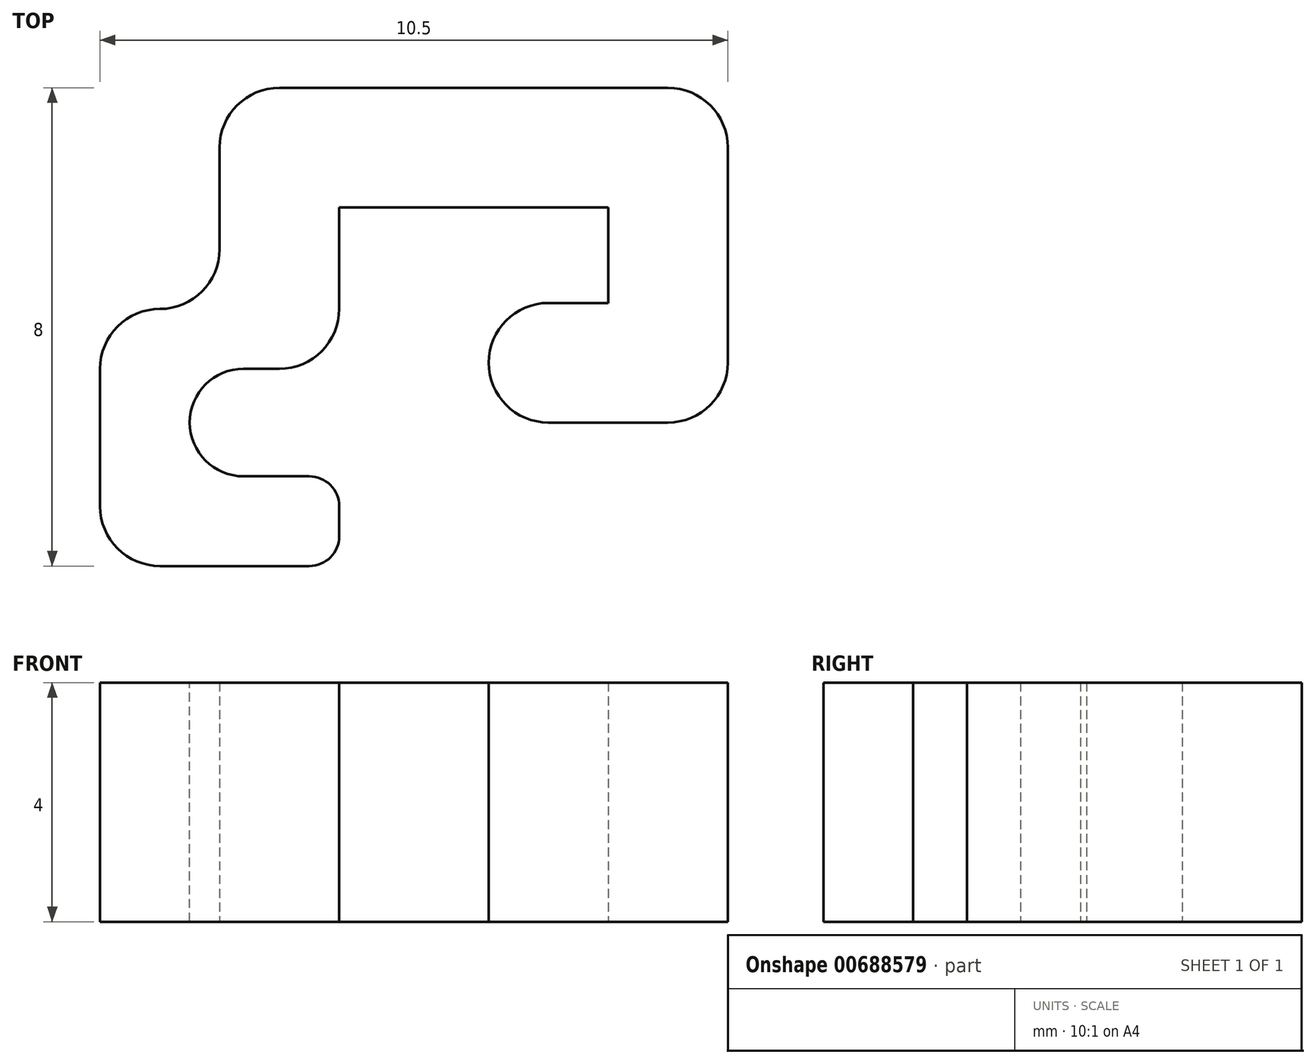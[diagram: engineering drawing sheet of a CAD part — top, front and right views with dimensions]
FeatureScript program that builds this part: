
annotation { "Feature Type Name" : "Feature", "Feature Type Description" : "" }
export const myFeature = defineFeature(function(context is Context, id is Id, definition is map)
    precondition{}
    {
        {
            var Q0;
            Q0=qCreatedBy(makeId("Top.planeOp"),FACE);
            var sketch = newSketch(context, id + "F0", { "sketchPlane" : qUnion([Q0])});
            skLineSegment(sketch, "E0", {"start": v(0, 0) * mm, "end": v(4.5, 0) * mm});
            skLineSegment(sketch, "E1", {"start": v(4.5, 0) * mm, "end": v(4.5, -1.6) * mm});
            skLineSegment(sketch, "E2", {"start": v(4.5, -1.6) * mm, "end": v(2.5, -1.6) * mm});
            skLineSegment(sketch, "E3", {"start": v(-2, 2) * mm, "end": v(6.5, 2) * mm});
            skLineSegment(sketch, "E4", {"start": v(6.5, 2) * mm, "end": v(6.5, -3.6) * mm});
            skLineSegment(sketch, "E5", {"start": v(6.5, -3.6) * mm, "end": v(2.5, -3.6) * mm});
            skLineSegment(sketch, "E6", {"start": v(2.5, -3.6) * mm, "end": v(2.5, -1.6) * mm});
            skLineSegment(sketch, "E7", {"start": v(0, 0) * mm, "end": v(0, -2.7) * mm});
            skLineSegment(sketch, "E8", {"start": v(0, -2.7) * mm, "end": v(-2.5, -2.7) * mm});
            skLineSegment(sketch, "E9", {"start": v(-2.5, -2.7) * mm, "end": v(-2.5, -4.5) * mm});
            skLineSegment(sketch, "E10", {"start": v(-2.5, -4.5) * mm, "end": v(0, -4.5) * mm});
            skLineSegment(sketch, "E11", {"start": v(0, -4.5) * mm, "end": v(0, -6) * mm});
            skLineSegment(sketch, "E12", {"start": v(0, -6) * mm, "end": v(-4, -6) * mm});
            skLineSegment(sketch, "E13", {"start": v(-4, -6) * mm, "end": v(-4, -1.7) * mm});
            skLineSegment(sketch, "E14", {"start": v(-4, -1.7) * mm, "end": v(-2, -1.7) * mm});
            skLineSegment(sketch, "E15", {"start": v(-2, -1.7) * mm, "end": v(-2, 2) * mm});
            skSolve(sketch);
        }
        {
            var Q0;
            Q0 = qSketchRegion(id + "F0", true);
            extrude(context, id + "F1", {"entities" : qUnion([Q0]), "depth" : 4 * mm, "offsetDistance" : 25 * mm});
        }
        {
            var Q0;
            Q0=makeQuery(id+"F1.opExtrude","SWEPT_EDGE",EDGE,{"disambiguationData":[OSD([sQuery(id+"F0.wireOp",EDGE,"E4"),sQuery(id+"F0.wireOp",EDGE,"E5")])]});
            var Q1;
            Q1=makeQuery(id+"F1.opExtrude","SWEPT_EDGE",EDGE,{"disambiguationData":[OSD([sQuery(id+"F0.wireOp",EDGE,"E3"),sQuery(id+"F0.wireOp",EDGE,"E4")])]});
            var Q2;
            Q2=makeQuery(id+"F1.opExtrude","SWEPT_EDGE",EDGE,{"disambiguationData":[OSD([sQuery(id+"F0.wireOp",EDGE,"E3"),sQuery(id+"F0.wireOp",EDGE,"E15")])]});
            var Q3;
            Q3=makeQuery(id+"F1.opExtrude","SWEPT_EDGE",EDGE,{"disambiguationData":[OSD([sQuery(id+"F0.wireOp",EDGE,"E14"),sQuery(id+"F0.wireOp",EDGE,"E15")])]});
            var Q4;
            Q4=makeQuery(id+"F1.opExtrude","SWEPT_EDGE",EDGE,{"disambiguationData":[OSD([sQuery(id+"F0.wireOp",EDGE,"E13"),sQuery(id+"F0.wireOp",EDGE,"E14")])]});
            var Q5;
            Q5=makeQuery(id+"F1.opExtrude","SWEPT_EDGE",EDGE,{"disambiguationData":[OSD([sQuery(id+"F0.wireOp",EDGE,"E12"),sQuery(id+"F0.wireOp",EDGE,"E13")])]});
            var Q6;
            Q6=makeQuery(id+"F1.opExtrude","SWEPT_EDGE",EDGE,{"disambiguationData":[OSD([sQuery(id+"F0.wireOp",EDGE,"E5"),sQuery(id+"F0.wireOp",EDGE,"E6")])]});
            var Q7;
            Q7=makeQuery(id+"F1.opExtrude","SWEPT_EDGE",EDGE,{"disambiguationData":[OSD([sQuery(id+"F0.wireOp",EDGE,"E7"),sQuery(id+"F0.wireOp",EDGE,"E8")])]});
            var Q8;
            Q8=makeQuery(id+"F1.opExtrude","SWEPT_EDGE",EDGE,{"disambiguationData":[OSD([sQuery(id+"F0.wireOp",EDGE,"E2"),sQuery(id+"F0.wireOp",EDGE,"E6")])]});
            fillet(context, id + "F2", {"entities" : qUnion([Q0, Q1, Q2, Q3, Q4, Q5, Q6, Q7, Q8]), "radius" : 1 * mm, "tangentPropagation" : true, "allowEdgeOverflow" : false});
        }
        {
            var Q0;
            Q0=makeQuery(id+"F1.opExtrude","SWEPT_EDGE",EDGE,{"disambiguationData":[OSD([sQuery(id+"F0.wireOp",EDGE,"E8"),sQuery(id+"F0.wireOp",EDGE,"E9")])]});
            var Q1;
            Q1=makeQuery(id+"F1.opExtrude","SWEPT_EDGE",EDGE,{"disambiguationData":[OSD([sQuery(id+"F0.wireOp",EDGE,"E9"),sQuery(id+"F0.wireOp",EDGE,"E10")])]});
            fillet(context, id + "F3", {"entities" : qUnion([Q0, Q1]), "radius" : (1.8 / 2) * mm, "tangentPropagation" : true, "allowEdgeOverflow" : false});
        }
        {
            var Q0;
            Q0=makeQuery(id+"F1.opExtrude","SWEPT_EDGE",EDGE,{"disambiguationData":[OSD([sQuery(id+"F0.wireOp",EDGE,"E11"),sQuery(id+"F0.wireOp",EDGE,"E12")])]});
            var Q1;
            Q1=makeQuery(id+"F1.opExtrude","SWEPT_EDGE",EDGE,{"disambiguationData":[OSD([sQuery(id+"F0.wireOp",EDGE,"E10"),sQuery(id+"F0.wireOp",EDGE,"E11")])]});
            fillet(context, id + "F4", {"entities" : qUnion([Q0, Q1]), "radius" : 0.5 * mm, "tangentPropagation" : true, "allowEdgeOverflow" : false});
        }
    });
